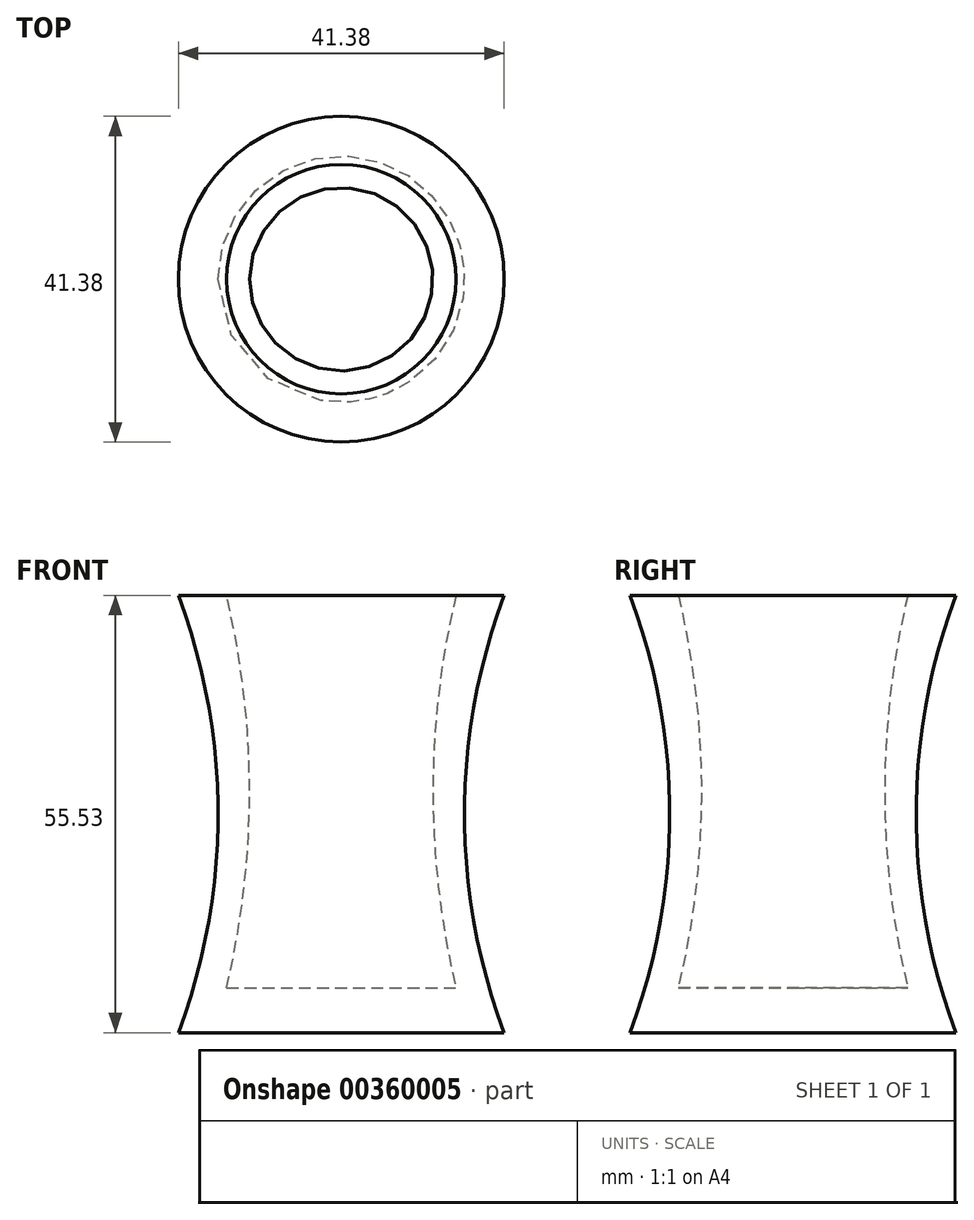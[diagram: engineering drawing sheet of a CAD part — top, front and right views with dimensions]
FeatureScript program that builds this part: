
annotation { "Feature Type Name" : "Feature", "Feature Type Description" : "" }
export const myFeature = defineFeature(function(context is Context, id is Id, definition is map)
    precondition{}
    {
        {
            var Q0;
            Q0=qCreatedBy(makeId("Front.planeOp"),FACE);
            var sketch = newSketch(context, id + "F0", { "sketchPlane" : qUnion([Q0])});
            skLineSegment(sketch, "E0", {"start": v(0, 0) * mm, "end": v(-20.7, 0) * mm});
            skArc(sketch, "E1", {"start": v(-20.7, 0) * mm, "mid": v(-15.65, 27.76) * mm, "end": v(-20.7, 55.53) * mm});
            skLineSegment(sketch, "E2", {"start": v(-20.7, 55.53) * mm, "end": v(-14.57, 55.53) * mm});
            skLineSegment(sketch, "E3", {"start": v(0, 0) * mm, "end": v(0, 55.82) * mm});
            skLineSegment(sketch, "E4", {"start": v(-14.57, 5.68) * mm, "end": v(0, 5.68) * mm});
            skArc(sketch, "E5", {"start": v(-14.57, 5.68) * mm, "mid": v(-11.65, 30.6) * mm, "end": v(-14.57, 55.53) * mm});
            skSolve(sketch);
        }
        {
            var Q0;
            Q0 = qSketchRegion(id + "F0", true);
            var Q1;
            Q1=sQuery(id+"F0.wireOp",EDGE,"E3");
            revolve(context, id + "F1", {"entities" : qUnion([Q0]), "axis" : qUnion([Q1]), "revolveType" : RevolveType.FULL});
        }
    });
